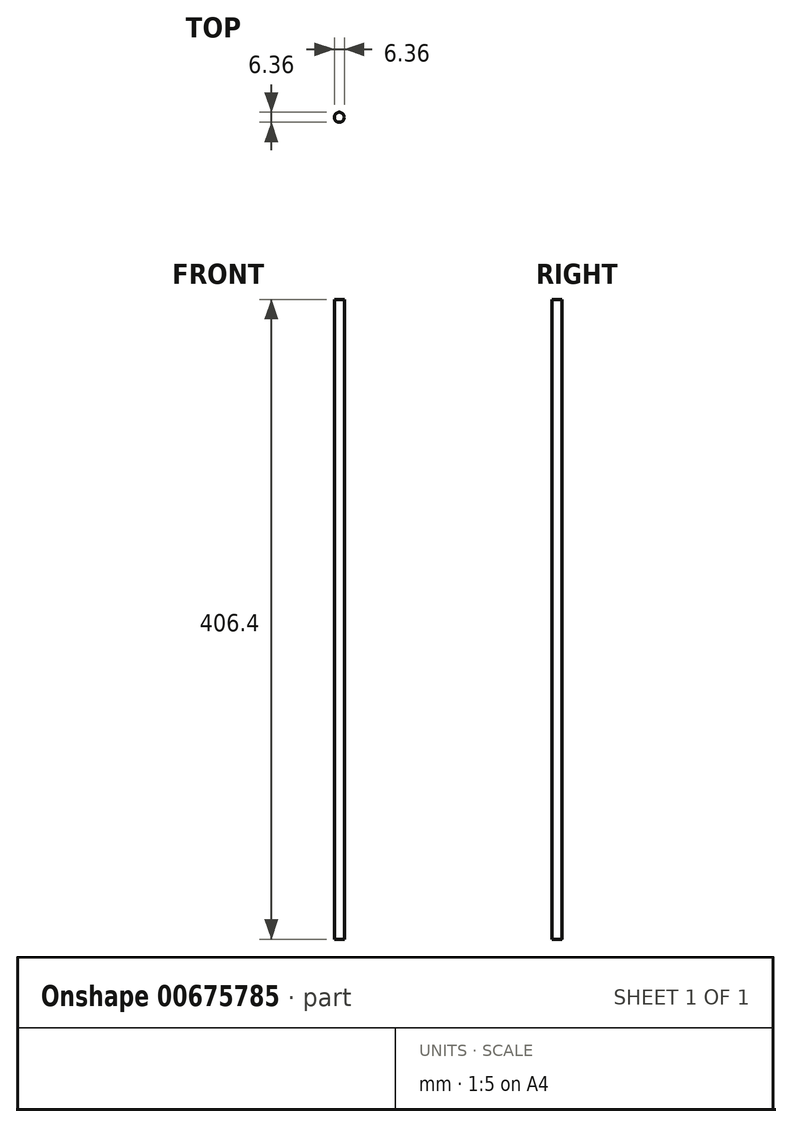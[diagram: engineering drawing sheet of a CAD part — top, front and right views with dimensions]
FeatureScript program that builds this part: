
annotation { "Feature Type Name" : "Feature", "Feature Type Description" : "" }
export const myFeature = defineFeature(function(context is Context, id is Id, definition is map)
    precondition{}
    {
        {
            var Q0;
            Q0=qCreatedBy(makeId("Top.planeOp"),FACE);
            var sketch = newSketch(context, id + "F0", { "sketchPlane" : qUnion([Q0])});
            skCircle(sketch, "E0", {"center": v(0, 0) * mm, "radius": 3.18 * mm});
            skSolve(sketch);
        }
        {
            var Q0;
            Q0 = qSketchRegion(id + "F0", true);
            extrude(context, id + "F1", {"entities" : qUnion([Q0]), "depth" : 406.4 * mm, "offsetDistance" : 25.4 * mm});
        }
    });
